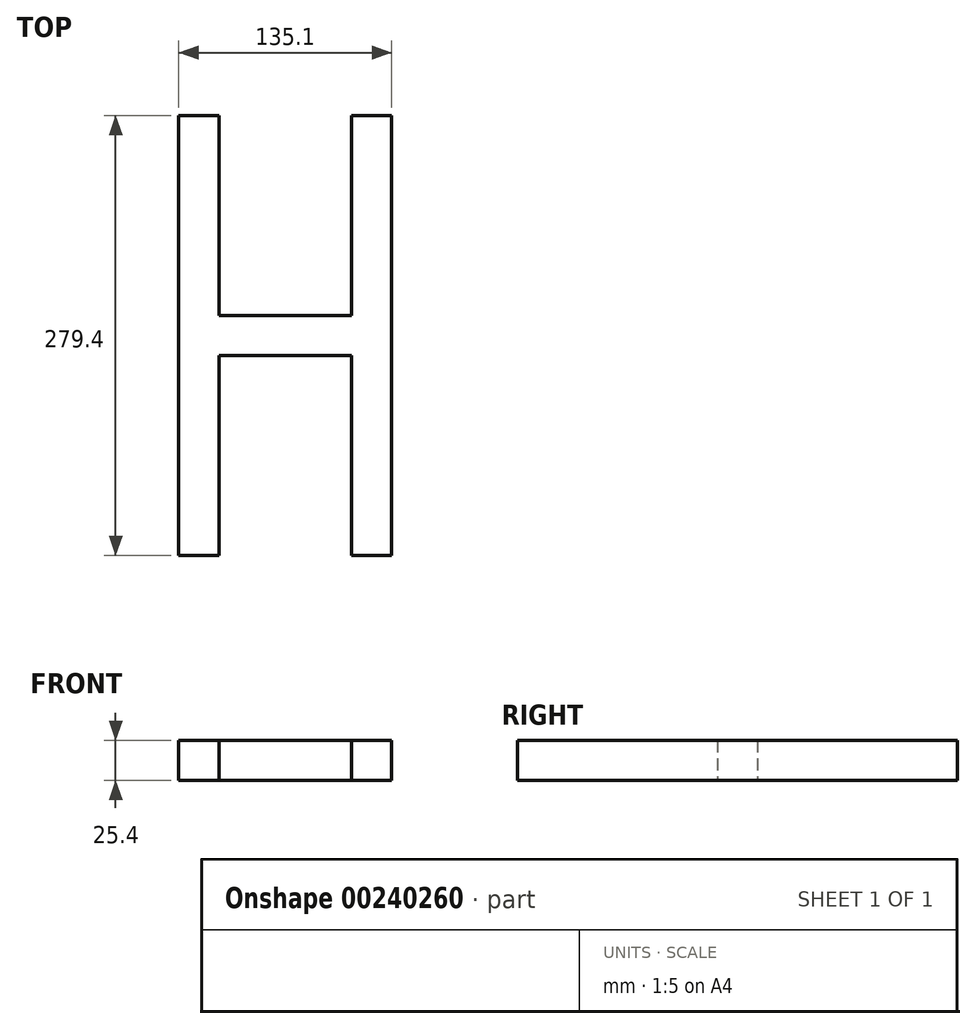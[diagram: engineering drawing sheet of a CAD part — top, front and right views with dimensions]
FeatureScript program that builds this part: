
annotation { "Feature Type Name" : "Feature", "Feature Type Description" : "" }
export const myFeature = defineFeature(function(context is Context, id is Id, definition is map)
    precondition{}
    {
        {
            var Q0;
            Q0=qCreatedBy(makeId("Top.planeOp"),FACE);
            var sketch = newSketch(context, id + "F0", { "sketchPlane" : qUnion([Q0])});
            skLineSegment(sketch, "E0", {"start": v(-87.12, 152.4) * mm, "end": v(-87.12, -127) * mm});
            skLineSegment(sketch, "E1", {"start": v(-87.12, -127) * mm, "end": v(-61.72, -127) * mm});
            skLineSegment(sketch, "E2", {"start": v(-61.72, -127) * mm, "end": v(-61.72, 0) * mm});
            skLineSegment(sketch, "E3", {"start": v(-61.72, 0) * mm, "end": v(22.58, 0) * mm});
            skLineSegment(sketch, "E4", {"start": v(22.58, 0) * mm, "end": v(22.58, -127) * mm});
            skLineSegment(sketch, "E5", {"start": v(22.58, -127) * mm, "end": v(47.98, -127) * mm});
            skLineSegment(sketch, "E6", {"start": v(47.98, -127) * mm, "end": v(47.98, 152.4) * mm});
            skLineSegment(sketch, "E7", {"start": v(22.58, 152.4) * mm, "end": v(47.98, 152.4) * mm});
            skLineSegment(sketch, "E8", {"start": v(22.58, 25.4) * mm, "end": v(22.58, 152.4) * mm});
            skLineSegment(sketch, "E9", {"start": v(22.58, 25.4) * mm, "end": v(-61.72, 25.4) * mm});
            skLineSegment(sketch, "E10", {"start": v(-61.72, 25.4) * mm, "end": v(-61.72, 152.4) * mm});
            skLineSegment(sketch, "E11", {"start": v(-61.72, 152.4) * mm, "end": v(-87.12, 152.4) * mm});
            skSolve(sketch);
        }
        {
            var Q0;
            Q0=makeQuery(id+"F0.imprint","IMPRINT",FACE,{"disambiguationData":[TD([[makeQuery(id+"F0.imprint","IMPRINT",EDGE,{"derivedFrom":sQuery(id+"F0.wireOp",EDGE,"E0")}),1.0]])]});
            extrude(context, id + "F1", {"entities" : qUnion([Q0]), "depth" : 25.4 * mm});
        }
    });
